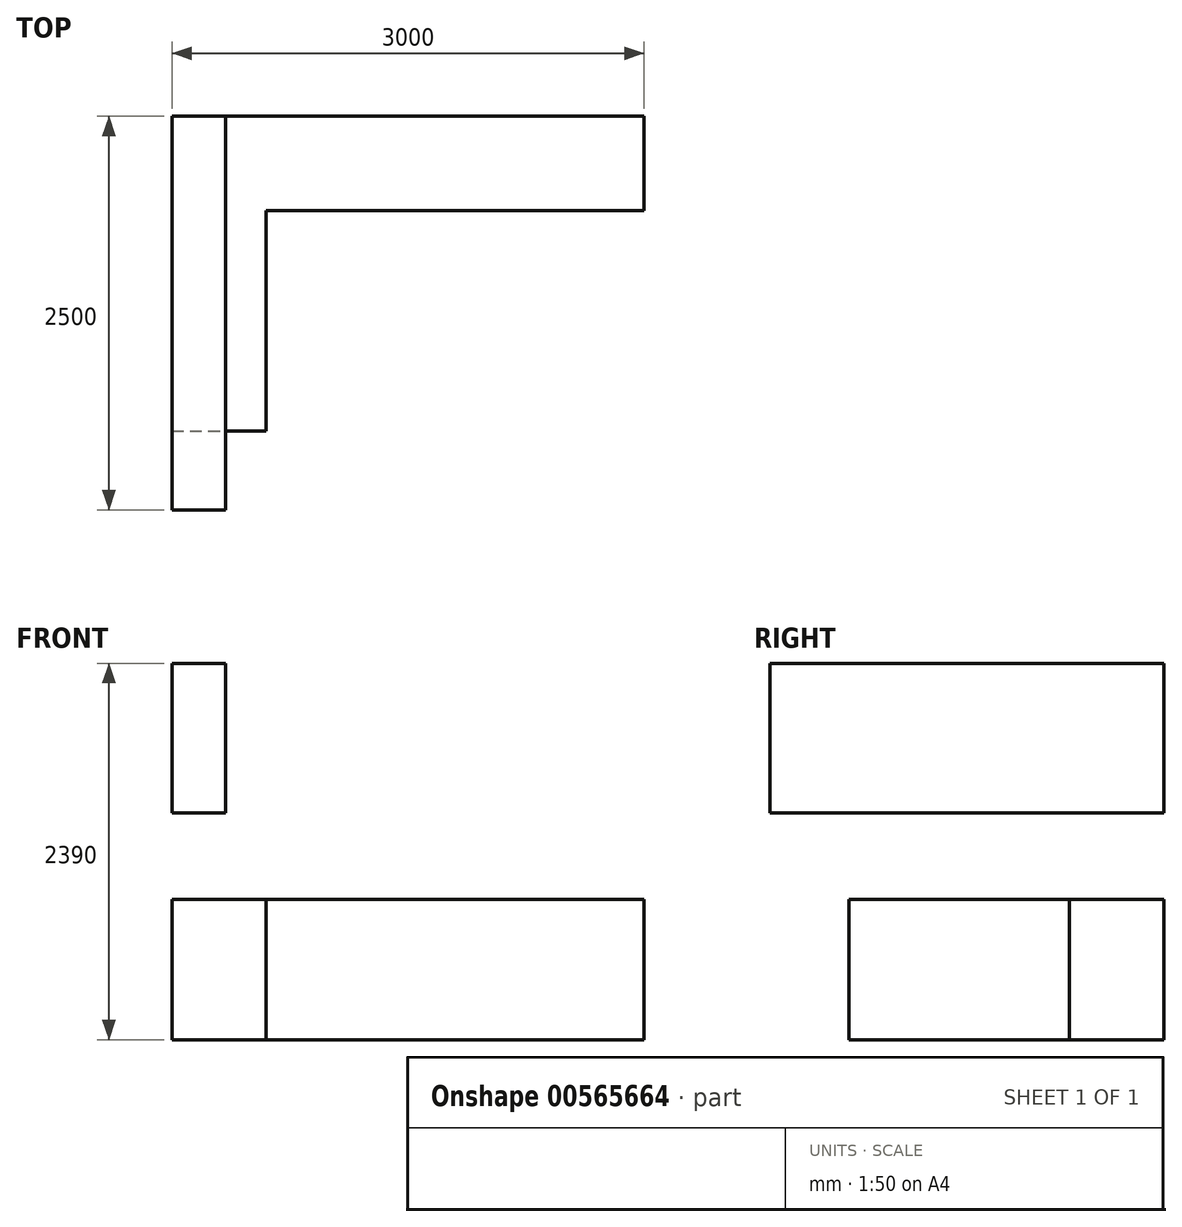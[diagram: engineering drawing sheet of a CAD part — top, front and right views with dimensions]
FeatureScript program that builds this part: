
annotation { "Feature Type Name" : "Feature", "Feature Type Description" : "" }
export const myFeature = defineFeature(function(context is Context, id is Id, definition is map)
    precondition{}
    {
        {
            var Q0;
            Q0=qCreatedBy(makeId("Top.planeOp"),FACE);
            var sketch = newSketch(context, id + "F0", { "sketchPlane" : qUnion([Q0])});
            skLineSegment(sketch, "E0", {"start": v(0, 0) * mm, "end": v(0, -2000) * mm});
            skLineSegment(sketch, "E1", {"start": v(0, -2000) * mm, "end": v(600, -2000) * mm});
            skLineSegment(sketch, "E2", {"start": v(600, -2000) * mm, "end": v(600, -600) * mm});
            skLineSegment(sketch, "E3", {"start": v(600, -600) * mm, "end": v(3000, -600) * mm});
            skLineSegment(sketch, "E4", {"start": v(3000, -600) * mm, "end": v(3000, 0) * mm});
            skLineSegment(sketch, "E5", {"start": v(3000, 0) * mm, "end": v(0, 0) * mm});
            skSolve(sketch);
        }
        {
            var Q0;
            Q0=makeQuery(id+"F0.imprint","IMPRINT",FACE,{"disambiguationData":[TD([[makeQuery(id+"F0.imprint","IMPRINT",EDGE,{"derivedFrom":sQuery(id+"F0.wireOp",EDGE,"E0")}),1.0]])]});
            extrude(context, id + "F1", {"entities" : qUnion([Q0]), "depth" : 890 * mm, "offsetDistance" : 25 * mm});
        }
        {
            var Q0;
            Q0=makeQuery(id+"F1.opExtrude","CAP_FACE",FACE,{"disambiguationData":[OSD([sQuery(id+"F0.wireOp",EDGE,"E0"),sQuery(id+"F0.wireOp",EDGE,"E1"),sQuery(id+"F0.wireOp",EDGE,"E2"),sQuery(id+"F0.wireOp",EDGE,"E3"),sQuery(id+"F0.wireOp",EDGE,"E4"),sQuery(id+"F0.wireOp",EDGE,"E5")])],"isStart":false});
            cPlane(context, id + "F2", {"entities" : qUnion([Q0]), "cplaneType" : CPlaneType.OFFSET, "offset" : 550 * mm, "width" : 150 * mm, "height" : 150 * mm});
        }
        {
            var Q0;
            Q0=qCreatedBy(id+"F2.planeOp",FACE);
            var sketch = newSketch(context, id + "F3", { "sketchPlane" : qUnion([Q0])});
            skLineSegment(sketch, "E6.bottom", {"start": v(0, 0) * mm, "end": v(340, 0) * mm});
            skLineSegment(sketch, "E6.top", {"start": v(0, -2500) * mm, "end": v(340, -2500) * mm});
            skLineSegment(sketch, "E6.left", {"start": v(0, 0) * mm, "end": v(0, -2500) * mm});
            skLineSegment(sketch, "E6.right", {"start": v(340, 0) * mm, "end": v(340, -2500) * mm});
            skSolve(sketch);
        }
        {
            var Q0;
            Q0 = qSketchRegion(id + "F3", true);
            extrude(context, id + "F4", {"entities" : qUnion([Q0]), "depth" : 950 * mm, "offsetDistance" : 25 * mm});
        }
    });
